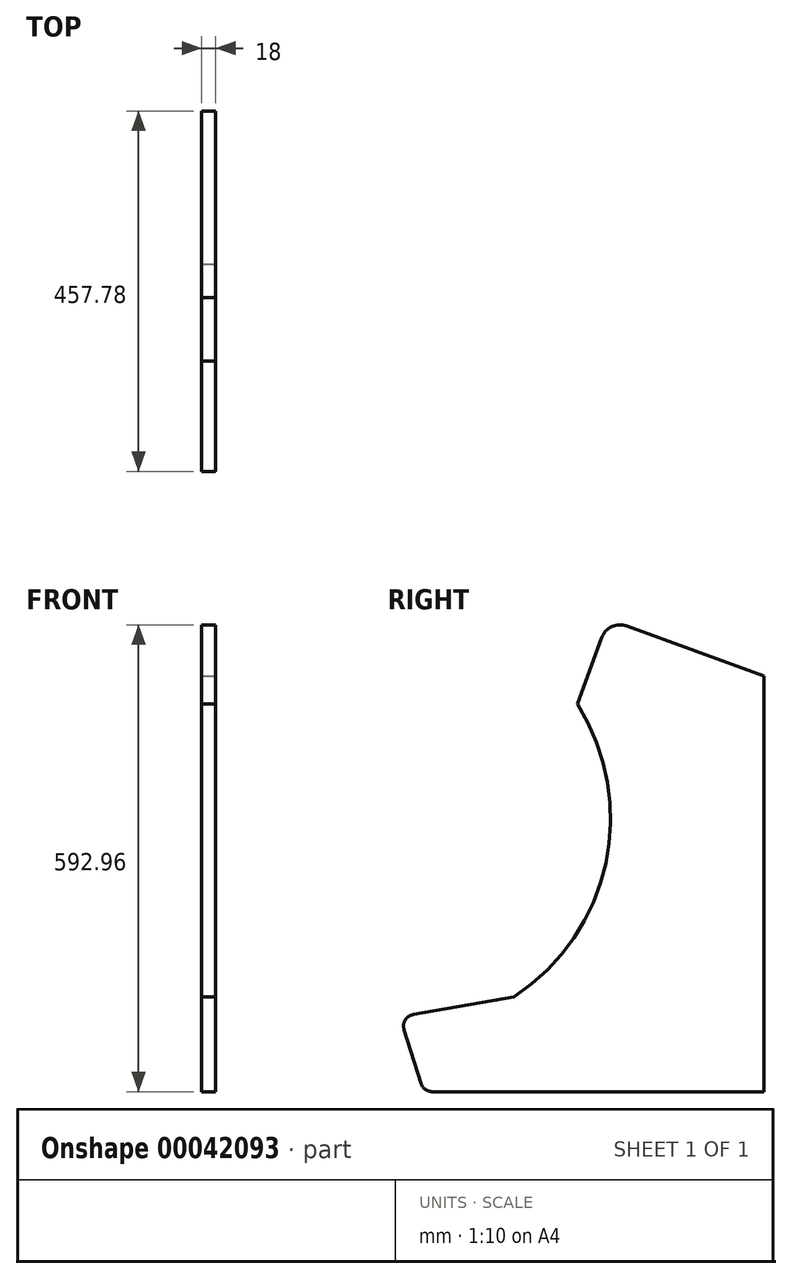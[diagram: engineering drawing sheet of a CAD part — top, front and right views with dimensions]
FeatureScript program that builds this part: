
annotation { "Feature Type Name" : "Feature", "Feature Type Description" : "" }
export const myFeature = defineFeature(function(context is Context, id is Id, definition is map)
    precondition{}
    {
        {
            var Q0;
            Q0=qCreatedBy(makeId("Right.planeOp"),FACE);
            var sketch = newSketch(context, id + "F0", { "sketchPlane" : qUnion([Q0])});
            skLineSegment(sketch, "E0", {"start": v(20.16, 27.2) * mm, "end": v(0.4, 34.39) * mm});
            skLineSegment(sketch, "E1", {"start": v(0.4, 34.39) * mm, "end": v(-3.52, 23.62) * mm});
            skLineSegment(sketch, "E2", {"start": v(20.16, 27.2) * mm, "end": v(20.16, -25.61) * mm});
            skLineSegment(sketch, "E3", {"start": v(20.16, -25.61) * mm, "end": v(-23.07, -25.61) * mm});
            skLineSegment(sketch, "E4", {"start": v(-23.07, -25.61) * mm, "end": v(-26.07, -16.11) * mm});
            skLineSegment(sketch, "E5", {"start": v(-26.07, -16.11) * mm, "end": v(-11.6, -13.56) * mm});
            skPoint(sketch, "E6.second.point", {"position": v(-51.42, 6.17) * mm});
            skPoint(sketch, "E6.third.point", {"position": v(-37.65, -9.55) * mm});
            skArc(sketch, "E7", {"start": v(-11.6, -13.56) * mm, "mid": v(0.07, 3.37) * mm, "end": v(-3.52, 23.62) * mm});
            skLineSegment(sketch, "E8", {"start": v(-55.33, -16.11) * mm, "end": v(41.51, -16.11) * mm, "construction": true});
            skLineSegment(sketch, "E9", {"start": v(-11.88, 27.2) * mm, "end": v(42.18, 27.2) * mm, "construction": true});
            skLineSegment(sketch, "E10", {"start": v(20.16, 27.2) * mm, "end": v(20.16, -40.98) * mm, "construction": true});
            skLineSegment(sketch, "E11", {"start": v(20.16, -30.61) * mm, "end": v(-34.84, -30.61) * mm, "construction": true});
            skSolve(sketch);
        }
        {
            var Q0;
            Q0 = qSketchRegion(id + "F0", true);
            extrude(context, id + "F1", {"entities" : qUnion([Q0]), "oppositeDirection" : true, "depth" : 1.8 * mm});
        }
        {
            var Q0;
            Q0=makeQuery(id+"F1.opExtrude","SWEPT_EDGE",EDGE,{"disambiguationData":[OSD([sQuery(id+"F0.wireOp",EDGE,"E4"),sQuery(id+"F0.wireOp",EDGE,"E5")])]});
            var Q1;
            Q1=makeQuery(id+"F1.opExtrude","SWEPT_EDGE",EDGE,{"disambiguationData":[OSD([sQuery(id+"F0.wireOp",EDGE,"E3"),sQuery(id+"F0.wireOp",EDGE,"E4")])]});
            fillet(context, id + "F2", {"entities" : qUnion([Q0, Q1]), "radius" : 1.5 * mm, "tangentPropagation" : true, "allowEdgeOverflow" : false});
        }
        {
            var Q0;
            Q0=makeQuery(id+"F1.opExtrude","SWEPT_EDGE",EDGE,{"disambiguationData":[OSD([sQuery(id+"F0.wireOp",EDGE,"E0"),sQuery(id+"F0.wireOp",EDGE,"E1")])]});
            fillet(context, id + "F3", {"entities" : qUnion([Q0]), "radius" : 2.5 * mm, "tangentPropagation" : true, "allowEdgeOverflow" : false});
        }
        {
            var Q0;
            Q0=makeQuery(id+"F1.opExtrude","SWEPT_BODY",BODY,{"disambiguationData":[OSD([sQuery(id+"F0.wireOp",EDGE,"E0"),sQuery(id+"F0.wireOp",EDGE,"E1"),sQuery(id+"F0.wireOp",EDGE,"E2"),sQuery(id+"F0.wireOp",EDGE,"E3"),sQuery(id+"F0.wireOp",EDGE,"E4"),sQuery(id+"F0.wireOp",EDGE,"E5"),sQuery(id+"F0.wireOp",EDGE,"E7")])]});
            var Q1;
            Q1=makeQuery(id+"F1.opExtrude","CAP_VERTEX",VERTEX,{"disambiguationData":[OSD([sQuery(id+"F0.wireOp",EDGE,"E2"),sQuery(id+"F0.wireOp",EDGE,"E3")])],"isStart":true});
            transform(context, id + "F4", {"entities" : qUnion([Q0]), "transformType" : TransformType.SCALE_UNIFORMLY, "scale" : 10, "makeCopy" : false, "scalePoint" : qUnion([Q1])});
        }
    });
